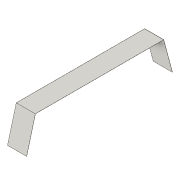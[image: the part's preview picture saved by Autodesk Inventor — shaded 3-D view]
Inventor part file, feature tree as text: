
AUTODESK INVENTOR PART (.ipt)
format: ipt  version: 2018 (Build 220112000, 112)  size: 92,672 bytes
history: native  units: in
note: dims shown in document units (in); Inventor stores cm internally (conversion verified against a paired STEP export)
features: plane x2, extrude x1, sketch x1
ambient origin geometry x8: Origin, YZ Plane, XZ Plane, XY Plane, X Axis, Y Axis, Z Axis, Center Point
bodies: Solid1 (feature_tree)
feature tree (4):
  extrude  "Extrusion1"  Depth=0.0747in
  plane  "Work Plane1"
  plane  "Work Plane2"
  sketch  "Sketch1"  dims[d6=17.0747in d7=0.0747in d8=0.0747in d9=105.0deg d10=8.5747in d11=8.5747in d12=72.0in d13=10.0in d14=0.0in d15=76.4005in]
